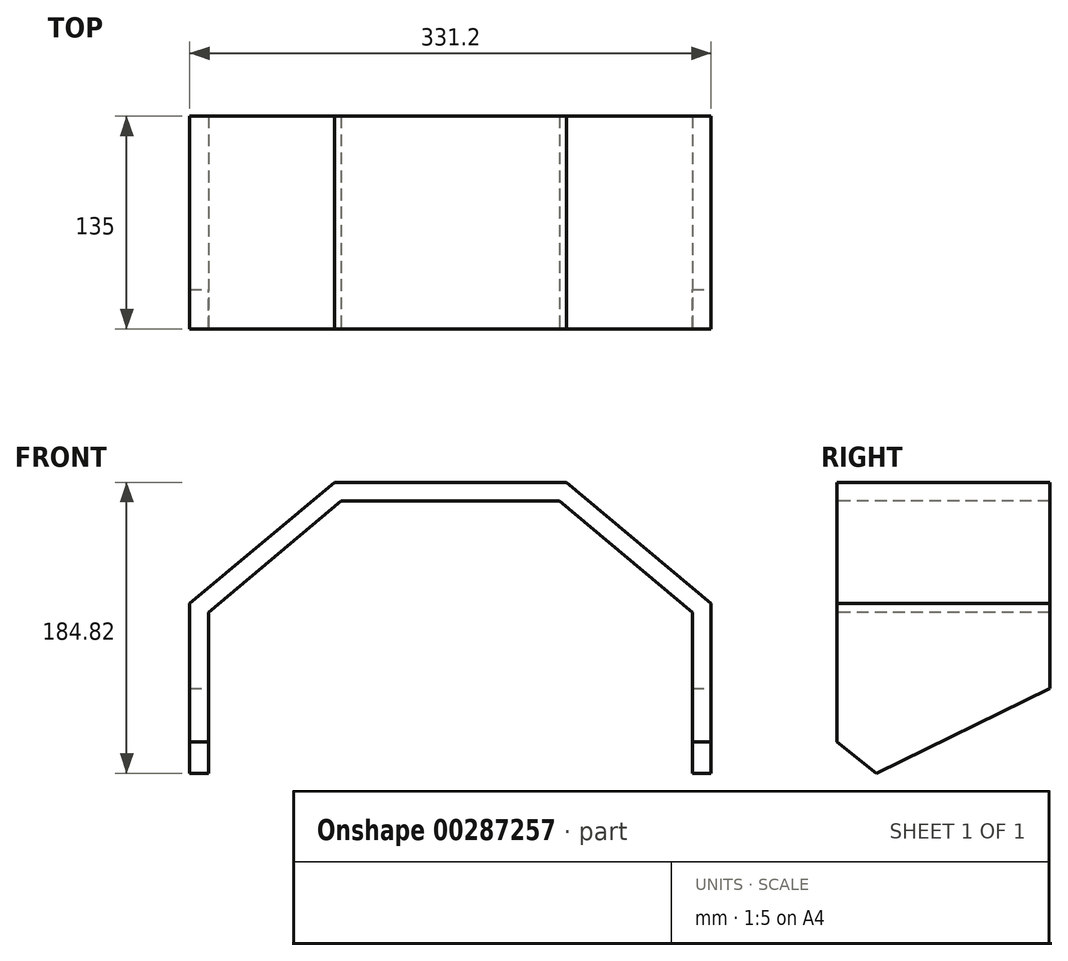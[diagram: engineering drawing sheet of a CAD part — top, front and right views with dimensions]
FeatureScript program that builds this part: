
annotation { "Feature Type Name" : "Feature", "Feature Type Description" : "" }
export const myFeature = defineFeature(function(context is Context, id is Id, definition is map)
    precondition{}
    {
        {
            var Q0;
            Q0=qCreatedBy(makeId("Front.planeOp"),FACE);
            var sketch = newSketch(context, id + "F0", { "sketchPlane" : qUnion([Q0])});
            skLineSegment(sketch, "E0", {"start": v(-69.37, 80.4) * mm, "end": v(69.37, 80.4) * mm});
            skLineSegment(sketch, "E1", {"start": v(-73.74, 92.4) * mm, "end": v(73.74, 92.4) * mm});
            skLineSegment(sketch, "E2", {"start": v(69.37, 80.4) * mm, "end": v(153.6, 9.72) * mm});
            skLineSegment(sketch, "E3", {"start": v(73.74, 92.4) * mm, "end": v(165.6, 15.32) * mm});
            skLineSegment(sketch, "E4", {"start": v(165.6, 15.32) * mm, "end": v(165.6, -92.4) * mm});
            skLineSegment(sketch, "E5", {"start": v(-69.37, 80.4) * mm, "end": v(-153.6, 9.72) * mm});
            skLineSegment(sketch, "E6", {"start": v(-73.74, 92.4) * mm, "end": v(-165.6, 15.32) * mm});
            skLineSegment(sketch, "E7", {"start": v(-153.6, 9.72) * mm, "end": v(-153.6, -92.4) * mm});
            skLineSegment(sketch, "E8", {"start": v(-165.6, 15.32) * mm, "end": v(-165.6, -92.4) * mm});
            skLineSegment(sketch, "E9", {"start": v(165.6, -92.4) * mm, "end": v(153.6, -92.4) * mm});
            skLineSegment(sketch, "E10", {"start": v(-153.6, -92.4) * mm, "end": v(-165.6, -92.4) * mm});
            skLineSegment(sketch, "E11", {"start": v(153.6, 9.72) * mm, "end": v(153.6, -92.4) * mm});
            skSolve(sketch);
        }
        {
            var Q0;
            Q0=makeQuery(id+"F0.imprint","IMPRINT",FACE,{"disambiguationData":[TD([[makeQuery(id+"F0.imprint","IMPRINT",EDGE,{"derivedFrom":sQuery(id+"F0.wireOp",EDGE,"E0")}),1.0]])]});
            extrude(context, id + "F1", {"entities" : qUnion([Q0]), "oppositeDirection" : true, "depth" : 135 * mm});
        }
        {
            var Q0;
            Q0=makeQuery(id+"F1.opExtrude","SWEPT_FACE",FACE,{"disambiguationData":[OSD([sQuery(id+"F0.wireOp",EDGE,"E4")])]});
            var sketch = newSketch(context, id + "F2", { "sketchPlane" : qUnion([Q0])});
            skLineSegment(sketch, "E12", {"start": v(25, -92.4) * mm, "end": v(135, -38.54) * mm});
            skLineSegment(sketch, "E13", {"start": v(135, -38.54) * mm, "end": v(135, -92.4) * mm});
            skLineSegment(sketch, "E14", {"start": v(135, -92.4) * mm, "end": v(25, -92.4) * mm});
            skLineSegment(sketch, "E15", {"start": v(25, -92.4) * mm, "end": v(0, -72.4) * mm});
            skLineSegment(sketch, "E16", {"start": v(0, -72.4) * mm, "end": v(0, -92.4) * mm});
            skLineSegment(sketch, "E17", {"start": v(0, -92.4) * mm, "end": v(25, -92.4) * mm});
            skSolve(sketch);
        }
        {
            var Q0;
            Q0=makeQuery(id+"F2.imprint","IMPRINT",FACE,{"disambiguationData":[TD([[makeQuery(id+"F2.imprint","IMPRINT",EDGE,{"derivedFrom":sQuery(id+"F2.wireOp",EDGE,"E15")}),1.0]])]});
            var Q1;
            Q1=makeQuery(id+"F2.imprint","IMPRINT",FACE,{"disambiguationData":[TD([[makeQuery(id+"F2.imprint","IMPRINT",EDGE,{"derivedFrom":sQuery(id+"F2.wireOp",EDGE,"E12")}),-1.0]])]});
            extrude(context, id + "F3", {"entities" : qUnion([Q0, Q1]), "operationType" : NewBodyOperationType.REMOVE, "oppositeDirection" : true, "depth" : 400 * mm});
        }
    });
